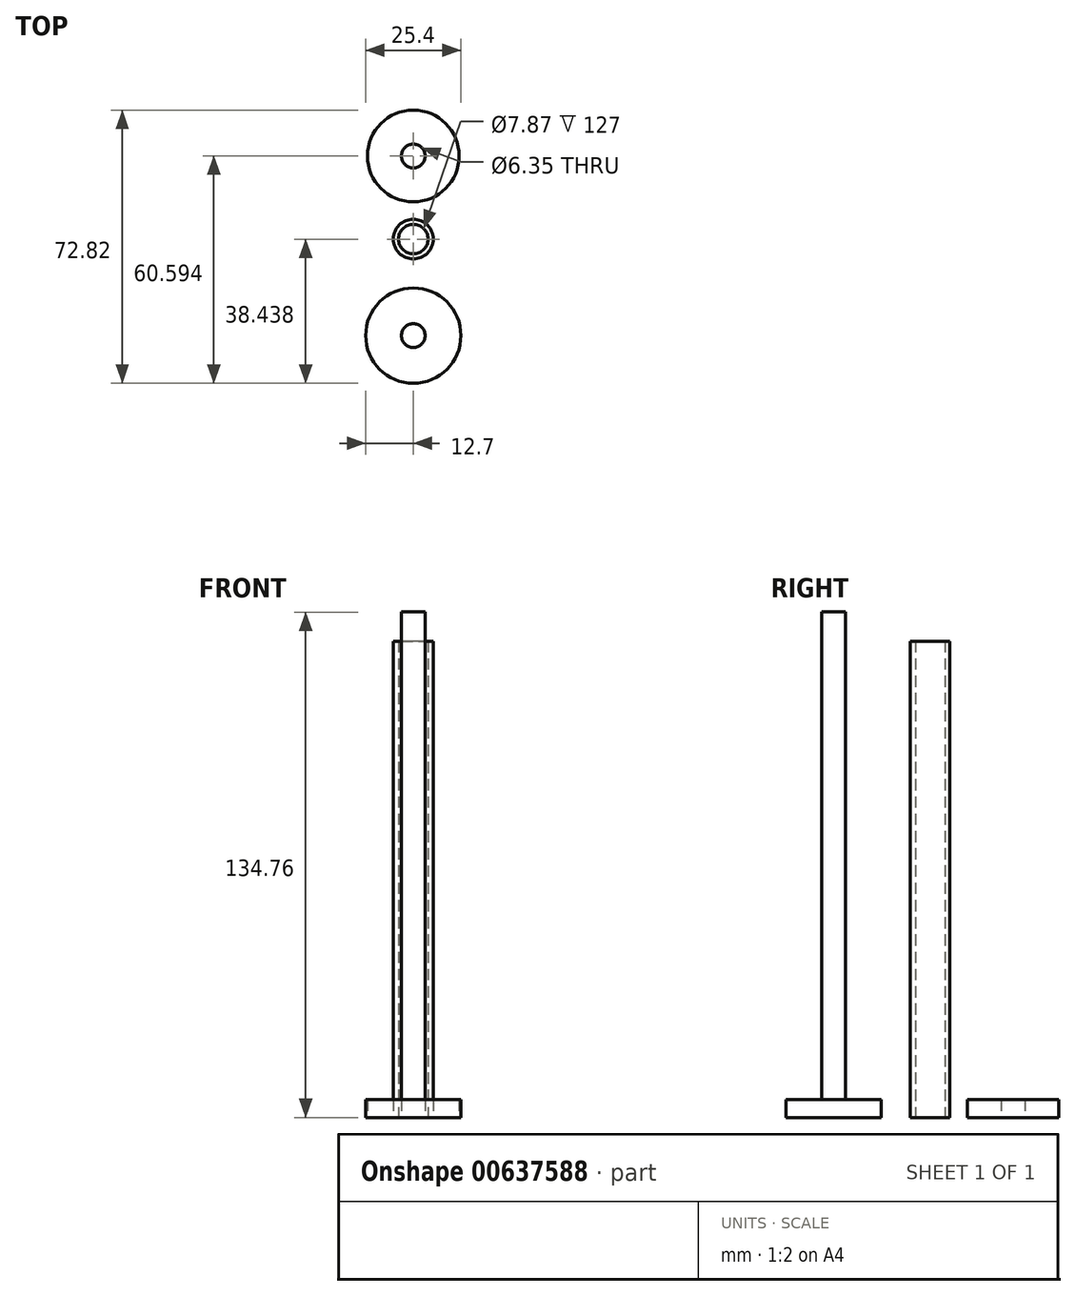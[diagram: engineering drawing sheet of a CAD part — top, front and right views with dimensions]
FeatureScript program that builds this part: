
annotation { "Feature Type Name" : "Feature", "Feature Type Description" : "" }
export const myFeature = defineFeature(function(context is Context, id is Id, definition is map)
    precondition{}
    {
        {
            var Q0;
            Q0=qCreatedBy(makeId("Top.planeOp"),FACE);
            var sketch = newSketch(context, id + "F0", { "sketchPlane" : qUnion([Q0])});
            skCircle(sketch, "E0", {"center": v(0, 0) * mm, "radius": 12.7 * mm});
            skSolve(sketch);
        }
        {
            var Q0;
            Q0 = qSketchRegion(id + "F0", true);
            extrude(context, id + "F1", {"entities" : qUnion([Q0]), "depth" : 4.76 * mm, "offsetDistance" : 25.4 * mm});
        }
        {
            var Q0;
            Q0=makeQuery(id+"F1.opExtrude","CAP_FACE",FACE,{"disambiguationData":[OSD([sQuery(id+"F0.wireOp",EDGE,"E0")])],"isStart":false});
            var sketch = newSketch(context, id + "F2", { "sketchPlane" : qUnion([Q0])});
            skCircle(sketch, "E1", {"center": v(0, 0) * mm, "radius": 3.17 * mm});
            skSolve(sketch);
        }
        {
            var Q0;
            Q0=makeQuery(id+"F2.imprint","IMPRINT",FACE,{"disambiguationData":[TD([[makeQuery(id+"F2.imprint","IMPRINT",EDGE,{"derivedFrom":sQuery(id+"F2.wireOp",EDGE,"E1")}),1.0]])]});
            var Q1;
            Q1=sQuery(id+"F2.wireOp",EDGE,"E1");
            extrude(context, id + "F3", {"entities" : qUnion([Q0]), "operationType" : NewBodyOperationType.ADD, "surfaceEntities" : qUnion([Q1]), "depth" : 130 * mm, "offsetDistance" : 25.4 * mm});
        }
        {
            var Q0;
            Q0=qCreatedBy(makeId("Top.planeOp"),FACE);
            var sketch = newSketch(context, id + "F4", { "sketchPlane" : qUnion([Q0])});
            skCircle(sketch, "E2", {"center": v(0, 47.9) * mm, "radius": 12.23 * mm});
            skSolve(sketch);
        }
        {
            var Q0;
            Q0=makeQuery(id+"F4.imprint","IMPRINT",FACE,{"disambiguationData":[TD([[makeQuery(id+"F4.imprint","IMPRINT",EDGE,{"derivedFrom":sQuery(id+"F4.wireOp",EDGE,"E2")}),1.0]])]});
            extrude(context, id + "F5", {"entities" : qUnion([Q0]), "depth" : 4.76 * mm, "offsetDistance" : 25.4 * mm});
        }
        {
            var Q0;
            Q0=makeQuery(id+"F5.opExtrude","CAP_FACE",FACE,{"disambiguationData":[OSD([sQuery(id+"F4.wireOp",EDGE,"E2")])],"isStart":true});
            var sketch = newSketch(context, id + "F6", { "sketchPlane" : qUnion([Q0])});
            skCircle(sketch, "E3", {"center": v(0, -47.9) * mm, "radius": 3.18 * mm});
            skSolve(sketch);
        }
        {
            var Q0;
            Q0=makeQuery(id+"F6.imprint","IMPRINT",FACE,{"disambiguationData":[TD([[makeQuery(id+"F6.imprint","IMPRINT",EDGE,{"derivedFrom":sQuery(id+"F6.wireOp",EDGE,"E3")}),1.0]])]});
            var Q1;
            Q1=sQuery(id+"F6.wireOp",EDGE,"E3");
            extrude(context, id + "F7", {"entities" : qUnion([Q0]), "operationType" : NewBodyOperationType.REMOVE, "surfaceEntities" : qUnion([Q1]), "oppositeDirection" : true, "depth" : 6.8 * mm, "offsetDistance" : 25.4 * mm});
        }
        {
            var Q0;
            Q0=qCreatedBy(makeId("Top.planeOp"),FACE);
            var sketch = newSketch(context, id + "F8", { "sketchPlane" : qUnion([Q0])});
            skCircle(sketch, "E4", {"center": v(0, 25.74) * mm, "radius": 3.94 * mm});
            skCircle(sketch, "E5", {"center": v(0, 25.74) * mm, "radius": 5.3 * mm});
            skSolve(sketch);
        }
        {
            var Q0;
            Q0 = qSketchRegion(id + "F8", true);
            extrude(context, id + "F9", {"entities" : qUnion([Q0]), "depth" : 127 * mm, "offsetDistance" : 25.4 * mm});
        }
    });
